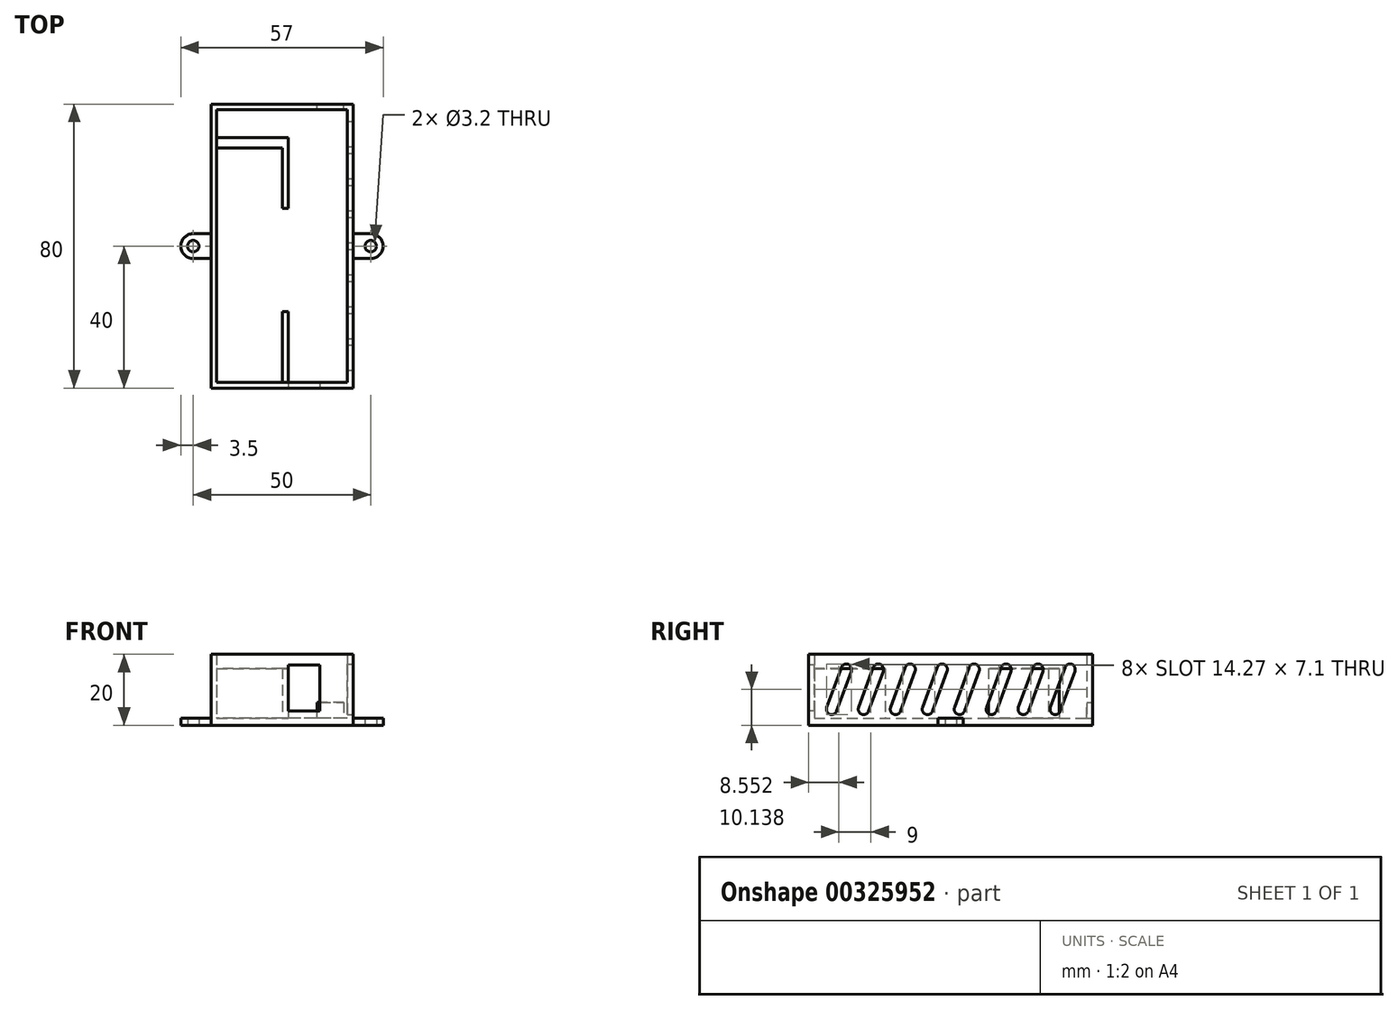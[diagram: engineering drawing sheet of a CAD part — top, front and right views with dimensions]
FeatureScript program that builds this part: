
annotation { "Feature Type Name" : "Feature", "Feature Type Description" : "" }
export const myFeature = defineFeature(function(context is Context, id is Id, definition is map)
    precondition{}
    {
        {
            var Q0;
            Q0=qCreatedBy(makeId("Top.planeOp"),FACE);
            var sketch = newSketch(context, id + "F0", { "sketchPlane" : qUnion([Q0])});
            skLineSegment(sketch, "E0.bottom", {"start": v(0, 0) * mm, "end": v(-40, 0) * mm});
            skLineSegment(sketch, "E0.top", {"start": v(0, 80) * mm, "end": v(-40, 80) * mm});
            skLineSegment(sketch, "E0.left", {"start": v(0, 0) * mm, "end": v(0, 80) * mm});
            skLineSegment(sketch, "E0.right", {"start": v(-40, 0) * mm, "end": v(-40, 80) * mm});
            skLineSegment(sketch, "E1.bottom", {"start": v(-1.6, 1.6) * mm, "end": v(-38.4, 1.6) * mm});
            skLineSegment(sketch, "E1.top", {"start": v(-1.6, 78.4) * mm, "end": v(-38.4, 78.4) * mm});
            skLineSegment(sketch, "E1.left", {"start": v(-1.6, 1.6) * mm, "end": v(-1.6, 78.4) * mm});
            skLineSegment(sketch, "E1.right", {"start": v(-38.4, 1.6) * mm, "end": v(-38.4, 78.4) * mm});
            skLineSegment(sketch, "E2", {"start": v(-40, 40) * mm, "end": v(0, 40) * mm, "construction": true});
            skLineSegment(sketch, "E3", {"start": v(-38.4, 70.6) * mm, "end": v(-18.3, 70.6) * mm});
            skLineSegment(sketch, "E4", {"start": v(-18.3, 70.6) * mm, "end": v(-18.3, 50.6) * mm});
            skLineSegment(sketch, "E5", {"start": v(-18.3, 50.6) * mm, "end": v(-19.9, 50.6) * mm});
            skLineSegment(sketch, "E6", {"start": v(-19.9, 50.6) * mm, "end": v(-19.9, 67.6) * mm});
            skLineSegment(sketch, "E7", {"start": v(-19.9, 67.6) * mm, "end": v(-38.4, 67.6) * mm});
            skLineSegment(sketch, "E8", {"start": v(-19.9, 1.6) * mm, "end": v(-19.9, 21.6) * mm});
            skLineSegment(sketch, "E9", {"start": v(-19.9, 21.6) * mm, "end": v(-18.3, 21.6) * mm});
            skLineSegment(sketch, "E10", {"start": v(-18.3, 21.6) * mm, "end": v(-18.3, 1.6) * mm});
            skCircle(sketch, "E11", {"center": v(-45, 40) * mm, "radius": 1.6 * mm});
            skCircle(sketch, "E12", {"center": v(5, 40) * mm, "radius": 1.6 * mm});
            skArc(sketch, "E13", {"start": v(-45, 43.5) * mm, "mid": v(-48.5, 40) * mm, "end": v(-45, 36.5) * mm});
            skArc(sketch, "E14", {"start": v(5, 36.5) * mm, "mid": v(8.5, 40) * mm, "end": v(5, 43.5) * mm});
            skLineSegment(sketch, "E15", {"start": v(-45, 43.5) * mm, "end": v(-40, 43.5) * mm});
            skLineSegment(sketch, "E16", {"start": v(-45, 36.5) * mm, "end": v(-40, 36.5) * mm});
            skLineSegment(sketch, "E17", {"start": v(5, 36.5) * mm, "end": v(0, 36.5) * mm});
            skLineSegment(sketch, "E18", {"start": v(5, 43.5) * mm, "end": v(0, 43.5) * mm});
            skSolve(sketch);
        }
        {
            var Q0;
            Q0=makeQuery(id+"F0.imprint","IMPRINT",FACE,{"disambiguationData":[TD([[makeQuery(id+"F0.imprint","IMPRINT",EDGE,{"derivedFrom":sQuery(id+"F0.wireOp",EDGE,"E0.bottom")}),-1.0]])]});
            extrude(context, id + "F1", {"entities" : qUnion([Q0]), "depth" : 20 * mm});
        }
        {
            var Q0;
            {var subQ2=sQuery(id+"F0.wireOp",EDGE,"E1.top");Q0=makeQuery(id+"F0.imprint","IMPRINT",FACE,{"disambiguationData":[TD([[makeQuery(id+"F0.imprint","IMPRINT",EDGE,{"derivedFrom":subQ2}),1.0]])]});}
            extrude(context, id + "F2", {"entities" : qUnion([Q0]), "operationType" : NewBodyOperationType.ADD, "depth" : 2 * mm});
        }
        {
            var Q0;
            {var subQ0=sQuery(id+"F0.wireOp",EDGE,"E3");Q0=makeQuery(id+"F0.imprint","IMPRINT",FACE,{"disambiguationData":[TD([[makeQuery(id+"F0.imprint","IMPRINT",EDGE,{"derivedFrom":subQ0}),-1.0]])]});}
            var Q1;
            {var subQ0=sQuery(id+"F0.wireOp",EDGE,"E8");Q1=makeQuery(id+"F0.imprint","IMPRINT",FACE,{"disambiguationData":[TD([[makeQuery(id+"F0.imprint","IMPRINT",EDGE,{"derivedFrom":subQ0}),-1.0]])]});}
            extrude(context, id + "F3", {"entities" : qUnion([Q0, Q1]), "operationType" : NewBodyOperationType.ADD, "depth" : 16 * mm});
        }
        {
            var Q0;
            Q0=makeQuery(id+"F1.opExtrude","SWEPT_FACE",FACE,{"disambiguationData":[OSD([sQuery(id+"F0.wireOp",EDGE,"E0.bottom")])]});
            var sketch = newSketch(context, id + "F4", { "sketchPlane" : qUnion([Q0])});
            skLineSegment(sketch, "E19.bottom", {"start": v(-18.3, 4) * mm, "end": v(-9.3, 4) * mm});
            skLineSegment(sketch, "E19.top", {"start": v(-18.3, 17) * mm, "end": v(-9.3, 17) * mm});
            skLineSegment(sketch, "E19.left", {"start": v(-18.3, 4) * mm, "end": v(-18.3, 17) * mm});
            skLineSegment(sketch, "E19.right", {"start": v(-9.3, 4) * mm, "end": v(-9.3, 17) * mm});
            skSolve(sketch);
        }
        {
            var Q0;
            Q0=makeQuery(id+"F4.imprint","IMPRINT",FACE,{"disambiguationData":[TD([[makeQuery(id+"F4.imprint","IMPRINT",EDGE,{"derivedFrom":sQuery(id+"F4.wireOp",EDGE,"E19.bottom")}),1.0]])]});
            extrude(context, id + "F5", {"entities" : qUnion([Q0]), "operationType" : NewBodyOperationType.REMOVE, "oppositeDirection" : true, "depth" : 10 * mm});
        }
        {
            var Q0;
            Q0=makeQuery(id+"F1.opExtrude","SWEPT_FACE",FACE,{"disambiguationData":[OSD([sQuery(id+"F0.wireOp",EDGE,"E0.left")])]});
            var sketch = newSketch(context, id + "F6", { "sketchPlane" : qUnion([Q0])});
            skArc(sketch, "E20", {"start": v(5.1, 5.01) * mm, "mid": v(5.99, 3.1) * mm, "end": v(7.9, 3.99) * mm});
            skArc(sketch, "E21", {"start": v(12.01, 15.26) * mm, "mid": v(11.12, 17.19) * mm, "end": v(9.2, 16.29) * mm});
            skLineSegment(sketch, "E22", {"start": v(9.2, 16.29) * mm, "end": v(5.1, 5.01) * mm});
            skLineSegment(sketch, "E23", {"start": v(7.9, 3.99) * mm, "end": v(12.01, 15.26) * mm});
            skArc(sketch, "E24.1.0.0", {"start": v(21.01, 15.26) * mm, "mid": v(20.12, 17.19) * mm, "end": v(18.2, 16.29) * mm});
            skLineSegment(sketch, "E24.1.0.1", {"start": v(16.9, 3.99) * mm, "end": v(21.01, 15.26) * mm});
            skLineSegment(sketch, "E24.1.0.2", {"start": v(18.2, 16.29) * mm, "end": v(14.1, 5.01) * mm});
            skArc(sketch, "E24.1.0.3", {"start": v(14.1, 5.01) * mm, "mid": v(14.99, 3.1) * mm, "end": v(16.9, 3.99) * mm});
            skArc(sketch, "E24.2.0.0", {"start": v(30.01, 15.26) * mm, "mid": v(29.12, 17.19) * mm, "end": v(27.2, 16.29) * mm});
            skLineSegment(sketch, "E24.2.0.1", {"start": v(25.9, 3.99) * mm, "end": v(30.01, 15.26) * mm});
            skLineSegment(sketch, "E24.2.0.2", {"start": v(27.2, 16.29) * mm, "end": v(23.1, 5.01) * mm});
            skArc(sketch, "E24.2.0.3", {"start": v(23.1, 5.01) * mm, "mid": v(23.99, 3.1) * mm, "end": v(25.9, 3.99) * mm});
            skLineSegment(sketch, "E24.direction1", {"start": v(9.2, 16.29) * mm, "end": v(18.2, 16.29) * mm, "construction": true});
            skArc(sketch, "E25.0.3.0", {"start": v(39.01, 15.26) * mm, "mid": v(38.12, 17.19) * mm, "end": v(36.2, 16.29) * mm});
            skLineSegment(sketch, "E25.4.3.0", {"start": v(34.9, 3.99) * mm, "end": v(39.01, 15.26) * mm});
            skLineSegment(sketch, "E25.7.3.0", {"start": v(36.2, 16.29) * mm, "end": v(32.1, 5.01) * mm});
            skArc(sketch, "E25.10.3.0", {"start": v(32.1, 5.01) * mm, "mid": v(32.99, 3.1) * mm, "end": v(34.9, 3.99) * mm});
            skArc(sketch, "E25.0.4.0", {"start": v(48.01, 15.26) * mm, "mid": v(47.12, 17.19) * mm, "end": v(45.2, 16.29) * mm});
            skLineSegment(sketch, "E25.4.4.0", {"start": v(43.9, 3.99) * mm, "end": v(48.01, 15.26) * mm});
            skLineSegment(sketch, "E25.7.4.0", {"start": v(45.2, 16.29) * mm, "end": v(41.1, 5.01) * mm});
            skArc(sketch, "E25.10.4.0", {"start": v(41.1, 5.01) * mm, "mid": v(41.99, 3.1) * mm, "end": v(43.9, 3.99) * mm});
            skArc(sketch, "E25.0.5.0", {"start": v(57.01, 15.26) * mm, "mid": v(56.12, 17.19) * mm, "end": v(54.2, 16.29) * mm});
            skLineSegment(sketch, "E25.4.5.0", {"start": v(52.9, 3.99) * mm, "end": v(57.01, 15.26) * mm});
            skLineSegment(sketch, "E25.7.5.0", {"start": v(54.2, 16.29) * mm, "end": v(50.1, 5.01) * mm});
            skArc(sketch, "E25.10.5.0", {"start": v(50.1, 5.01) * mm, "mid": v(50.99, 3.1) * mm, "end": v(52.9, 3.99) * mm});
            skArc(sketch, "E26.0.6.0", {"start": v(66.01, 15.26) * mm, "mid": v(65.12, 17.19) * mm, "end": v(63.2, 16.29) * mm});
            skLineSegment(sketch, "E26.4.6.0", {"start": v(61.9, 3.99) * mm, "end": v(66.01, 15.26) * mm});
            skLineSegment(sketch, "E26.7.6.0", {"start": v(63.2, 16.29) * mm, "end": v(59.1, 5.01) * mm});
            skArc(sketch, "E26.10.6.0", {"start": v(59.1, 5.01) * mm, "mid": v(59.99, 3.1) * mm, "end": v(61.9, 3.99) * mm});
            skArc(sketch, "E27.0.7.0", {"start": v(75.01, 15.26) * mm, "mid": v(74.12, 17.19) * mm, "end": v(72.2, 16.29) * mm});
            skLineSegment(sketch, "E27.4.7.0", {"start": v(70.9, 3.99) * mm, "end": v(75.01, 15.26) * mm});
            skLineSegment(sketch, "E27.7.7.0", {"start": v(72.2, 16.29) * mm, "end": v(68.1, 5.01) * mm});
            skArc(sketch, "E27.10.7.0", {"start": v(68.1, 5.01) * mm, "mid": v(68.99, 3.1) * mm, "end": v(70.9, 3.99) * mm});
            skSolve(sketch);
        }
        {
            var Q0;
            Q0=makeQuery(id+"F6.imprint","IMPRINT",FACE,{"disambiguationData":[TD([[makeQuery(id+"F6.imprint","IMPRINT",EDGE,{"derivedFrom":sQuery(id+"F6.wireOp",EDGE,"E20")}),1.0]])]});
            var Q1;
            Q1=makeQuery(id+"F6.imprint","IMPRINT",FACE,{"disambiguationData":[TD([[makeQuery(id+"F6.imprint","IMPRINT",EDGE,{"derivedFrom":sQuery(id+"F6.wireOp",EDGE,"E24.1.0.0")}),1.0]])]});
            var Q2;
            Q2=makeQuery(id+"F6.imprint","IMPRINT",FACE,{"disambiguationData":[TD([[makeQuery(id+"F6.imprint","IMPRINT",EDGE,{"derivedFrom":sQuery(id+"F6.wireOp",EDGE,"E24.2.0.0")}),1.0]])]});
            var Q3;
            Q3=makeQuery(id+"F6.imprint","IMPRINT",FACE,{"disambiguationData":[TD([[makeQuery(id+"F6.imprint","IMPRINT",EDGE,{"derivedFrom":sQuery(id+"F6.wireOp",EDGE,"E25.0.3.0")}),1.0]])]});
            var Q4;
            Q4=makeQuery(id+"F6.imprint","IMPRINT",FACE,{"disambiguationData":[TD([[makeQuery(id+"F6.imprint","IMPRINT",EDGE,{"derivedFrom":sQuery(id+"F6.wireOp",EDGE,"E25.0.4.0")}),1.0]])]});
            var Q5;
            Q5=makeQuery(id+"F6.imprint","IMPRINT",FACE,{"disambiguationData":[TD([[makeQuery(id+"F6.imprint","IMPRINT",EDGE,{"derivedFrom":sQuery(id+"F6.wireOp",EDGE,"E25.0.5.0")}),1.0]])]});
            var Q6;
            Q6=makeQuery(id+"F6.imprint","IMPRINT",FACE,{"disambiguationData":[TD([[makeQuery(id+"F6.imprint","IMPRINT",EDGE,{"derivedFrom":sQuery(id+"F6.wireOp",EDGE,"E26.0.6.0")}),1.0]])]});
            var Q7;
            Q7=makeQuery(id+"F6.imprint","IMPRINT",FACE,{"disambiguationData":[TD([[makeQuery(id+"F6.imprint","IMPRINT",EDGE,{"derivedFrom":sQuery(id+"F6.wireOp",EDGE,"E27.0.7.0")}),1.0]])]});
            extrude(context, id + "F7", {"entities" : qUnion([Q0, Q1, Q2, Q3, Q4, Q5, Q6, Q7]), "operationType" : NewBodyOperationType.REMOVE, "oppositeDirection" : true, "depth" : 5 * mm});
        }
        {
            var Q0;
            Q0=makeQuery(id+"F1.opExtrude","SWEPT_FACE",FACE,{"disambiguationData":[OSD([sQuery(id+"F0.wireOp",EDGE,"E0.top")])]});
            var sketch = newSketch(context, id + "F8", { "sketchPlane" : qUnion([Q0])});
            skLineSegment(sketch, "E28.bottom", {"start": v(2.6, 6.5) * mm, "end": v(10.1, 6.5) * mm});
            skLineSegment(sketch, "E28.top", {"start": v(2.6, 2) * mm, "end": v(10.1, 2) * mm});
            skLineSegment(sketch, "E28.left", {"start": v(2.6, 6.5) * mm, "end": v(2.6, 2) * mm});
            skLineSegment(sketch, "E28.right", {"start": v(10.1, 6.5) * mm, "end": v(10.1, 2) * mm});
            skSolve(sketch);
        }
        {
            var Q0;
            Q0=makeQuery(id+"F8.imprint","IMPRINT",FACE,{"disambiguationData":[TD([[makeQuery(id+"F8.imprint","IMPRINT",EDGE,{"derivedFrom":sQuery(id+"F8.wireOp",EDGE,"E28.bottom")}),-1.0]])]});
            extrude(context, id + "F9", {"entities" : qUnion([Q0]), "operationType" : NewBodyOperationType.REMOVE, "oppositeDirection" : true, "depth" : 5 * mm});
        }
        {
            var Q0;
            Q0=makeQuery(id+"F0.imprint","IMPRINT",FACE,{"disambiguationData":[TD([[makeQuery(id+"F0.imprint","IMPRINT",EDGE,{"derivedFrom":sQuery(id+"F0.wireOp",EDGE,"E11")}),-1.0]])]});
            var Q1;
            Q1=makeQuery(id+"F0.imprint","IMPRINT",FACE,{"disambiguationData":[TD([[makeQuery(id+"F0.imprint","IMPRINT",EDGE,{"derivedFrom":sQuery(id+"F0.wireOp",EDGE,"E12")}),-1.0]])]});
            extrude(context, id + "F10", {"entities" : qUnion([Q0, Q1]), "operationType" : NewBodyOperationType.ADD, "depth" : 2 * mm});
        }
    });
